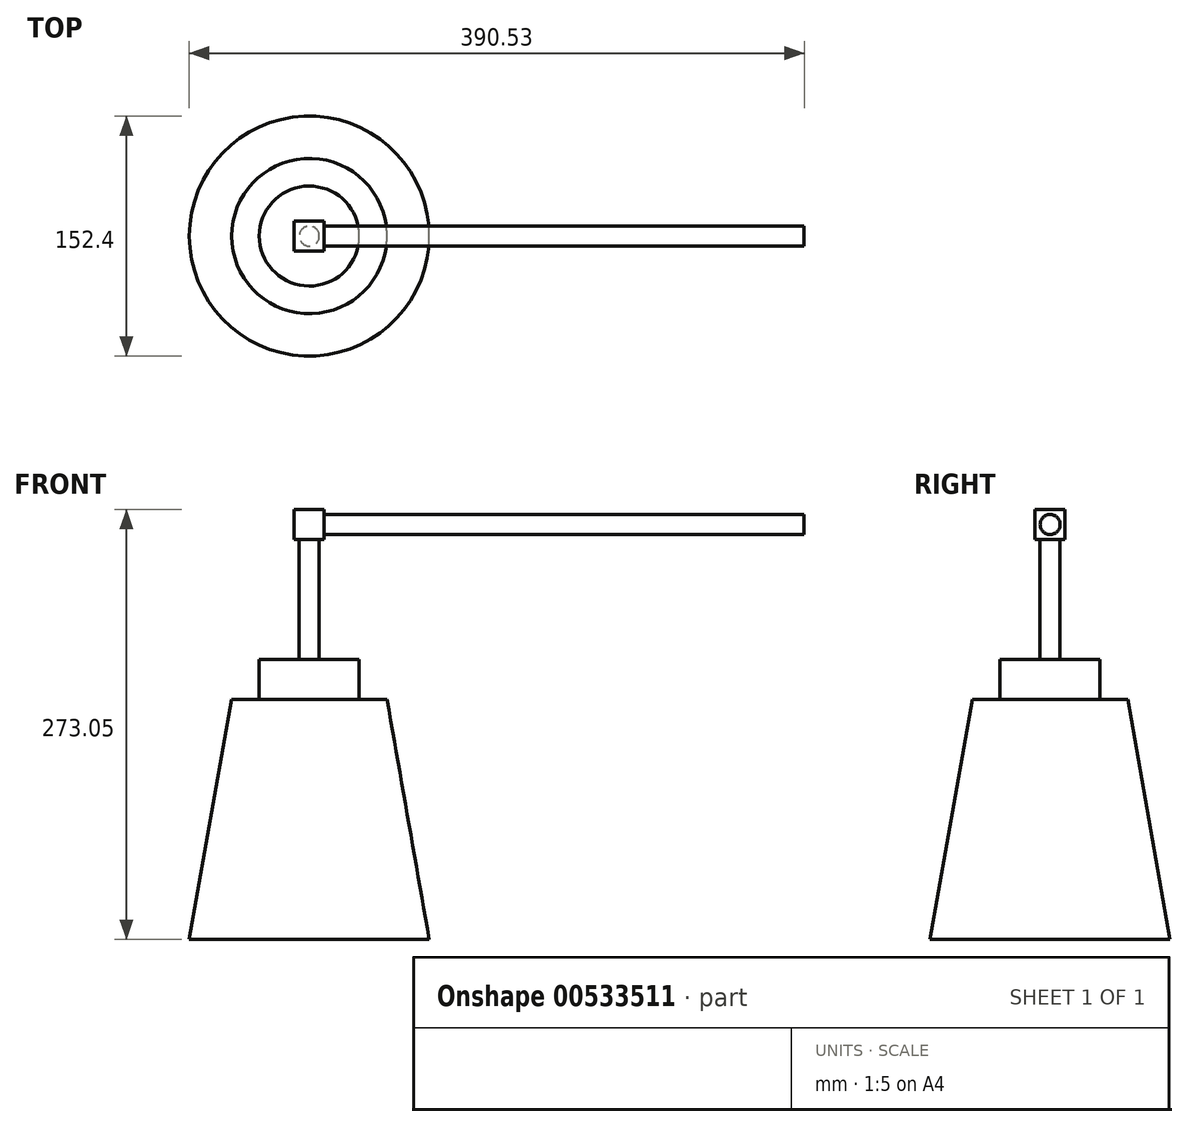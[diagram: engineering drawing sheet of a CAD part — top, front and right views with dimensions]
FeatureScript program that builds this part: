
annotation { "Feature Type Name" : "Feature", "Feature Type Description" : "" }
export const myFeature = defineFeature(function(context is Context, id is Id, definition is map)
    precondition{}
    {
        {
            var Q0;
            Q0=qCreatedBy(makeId("Top.planeOp"),FACE);
            var sketch = newSketch(context, id + "F0", { "sketchPlane" : qUnion([Q0])});
            skCircle(sketch, "E0", {"center": v(0, 0) * mm, "radius": 76.2 * mm});
            skSolve(sketch);
        }
        {
            var Q0;
            Q0=makeQuery(id+"F0.imprint","IMPRINT",FACE,{"disambiguationData":[TD([[makeQuery(id+"F0.imprint","IMPRINT",EDGE,{"derivedFrom":sQuery(id+"F0.wireOp",EDGE,"E0")}),1.0]])]});
            extrude(context, id + "F1", {"entities" : qUnion([Q0]), "depth" : 152.4 * mm, "offsetDistance" : 25.4 * mm, "hasDraft" : true, "draftAngle" : 10 * degree, "draftPullDirection" : true});
        }
        {
            var Q0;
            Q0=makeQuery(id+"F1.opExtrude","CAP_FACE",FACE,{"disambiguationData":[OSD([sQuery(id+"F0.wireOp",EDGE,"E0")])],"isStart":false});
            var sketch = newSketch(context, id + "F2", { "sketchPlane" : qUnion([Q0])});
            skCircle(sketch, "E1", {"center": v(0, 0) * mm, "radius": 31.75 * mm});
            skSolve(sketch);
        }
        {
            var Q0;
            Q0=makeQuery(id+"F2.imprint","IMPRINT",FACE,{"disambiguationData":[TD([[makeQuery(id+"F2.imprint","IMPRINT",EDGE,{"derivedFrom":sQuery(id+"F2.wireOp",EDGE,"E1")}),1.0]])]});
            extrude(context, id + "F3", {"entities" : qUnion([Q0]), "operationType" : NewBodyOperationType.ADD, "depth" : 25.4 * mm, "offsetDistance" : 25.4 * mm});
        }
        {
            var Q0;
            Q0=makeQuery(id+"F3.opExtrude","CAP_FACE",FACE,{"disambiguationData":[OSD([sQuery(id+"F2.wireOp",EDGE,"E1")])],"isStart":false});
            var sketch = newSketch(context, id + "F4", { "sketchPlane" : qUnion([Q0])});
            skCircle(sketch, "E2", {"center": v(0, 0) * mm, "radius": 6.35 * mm});
            skSolve(sketch);
        }
        {
            var Q0;
            Q0=makeQuery(id+"F4.imprint","IMPRINT",FACE,{"disambiguationData":[TD([[makeQuery(id+"F4.imprint","IMPRINT",EDGE,{"derivedFrom":sQuery(id+"F4.wireOp",EDGE,"E2")}),1.0]])]});
            extrude(context, id + "F5", {"entities" : qUnion([Q0]), "operationType" : NewBodyOperationType.ADD, "depth" : 76.2 * mm, "offsetDistance" : 25.4 * mm});
        }
        {
            var Q0;
            Q0=makeQuery(id+"F5.opExtrude","CAP_FACE",FACE,{"disambiguationData":[OSD([sQuery(id+"F4.wireOp",EDGE,"E2")])],"isStart":false});
            var sketch = newSketch(context, id + "F6", { "sketchPlane" : qUnion([Q0])});
            skLineSegment(sketch, "E3.bottom", {"start": v(9.53, -9.53) * mm, "end": v(-9.53, -9.53) * mm});
            skLineSegment(sketch, "E3.top", {"start": v(9.53, 9.53) * mm, "end": v(-9.53, 9.53) * mm});
            skLineSegment(sketch, "E3.left", {"start": v(9.53, -9.53) * mm, "end": v(9.53, 9.53) * mm});
            skLineSegment(sketch, "E3.right", {"start": v(-9.53, -9.53) * mm, "end": v(-9.53, 9.53) * mm});
            skPoint(sketch, "E3.middle", {"position": v(0, 0) * mm});
            skSolve(sketch);
        }
        {
            var Q0;
            Q0=makeQuery(id+"F6.imprint","IMPRINT",FACE,{"disambiguationData":[TD([[makeQuery(id+"F6.imprint","IMPRINT",EDGE,{"derivedFrom":sQuery(id+"F6.wireOp",EDGE,"E3.bottom")}),-1.0]])]});
            var Q1;
            Q1=makeQuery(id+"F6.imprint","IMPRINT",FACE,{"disambiguationData":[TD([[makeQuery(id+"F6.imprint","IMPRINT",EDGE,{"derivedFrom":makeQuery(id+"F5.opExtrude","CAP_EDGE",EDGE,{"disambiguationData":[OSD([sQuery(id+"F4.wireOp",EDGE,"E2")])],"isStart":false})}),1.0]])]});
            extrude(context, id + "F7", {"entities" : qUnion([Q0, Q1]), "operationType" : NewBodyOperationType.ADD, "flatOperationType" : FlatOperationType.REMOVE, "depth" : 19.05 * mm, "offsetDistance" : 25.4 * mm, "domain" : OperationDomain.MODEL});
        }
        {
            var Q0;
            Q0=makeQuery(id+"F7.opExtrude","SWEPT_FACE",FACE,{"disambiguationData":[OSD([sQuery(id+"F6.wireOp",EDGE,"E3.left")])]});
            var sketch = newSketch(context, id + "F8", { "sketchPlane" : qUnion([Q0])});
            skCircle(sketch, "E4", {"center": v(0, 263.53) * mm, "radius": 6.35 * mm});
            skPoint(sketch, "E4.centerSnap0", {"position": v(0, 254) * mm});
            skPoint(sketch, "E4.centerSnap1", {"position": v(-9.53, 263.53) * mm});
            skSolve(sketch);
        }
        {
            var Q0;
            Q0=makeQuery(id+"F8.imprint","IMPRINT",FACE,{"disambiguationData":[TD([[makeQuery(id+"F8.imprint","IMPRINT",EDGE,{"derivedFrom":sQuery(id+"F8.wireOp",EDGE,"E4")}),1.0]])]});
            extrude(context, id + "F9", {"entities" : qUnion([Q0]), "operationType" : NewBodyOperationType.ADD, "depth" : 304.8 * mm, "offsetDistance" : 25.4 * mm});
        }
    });
